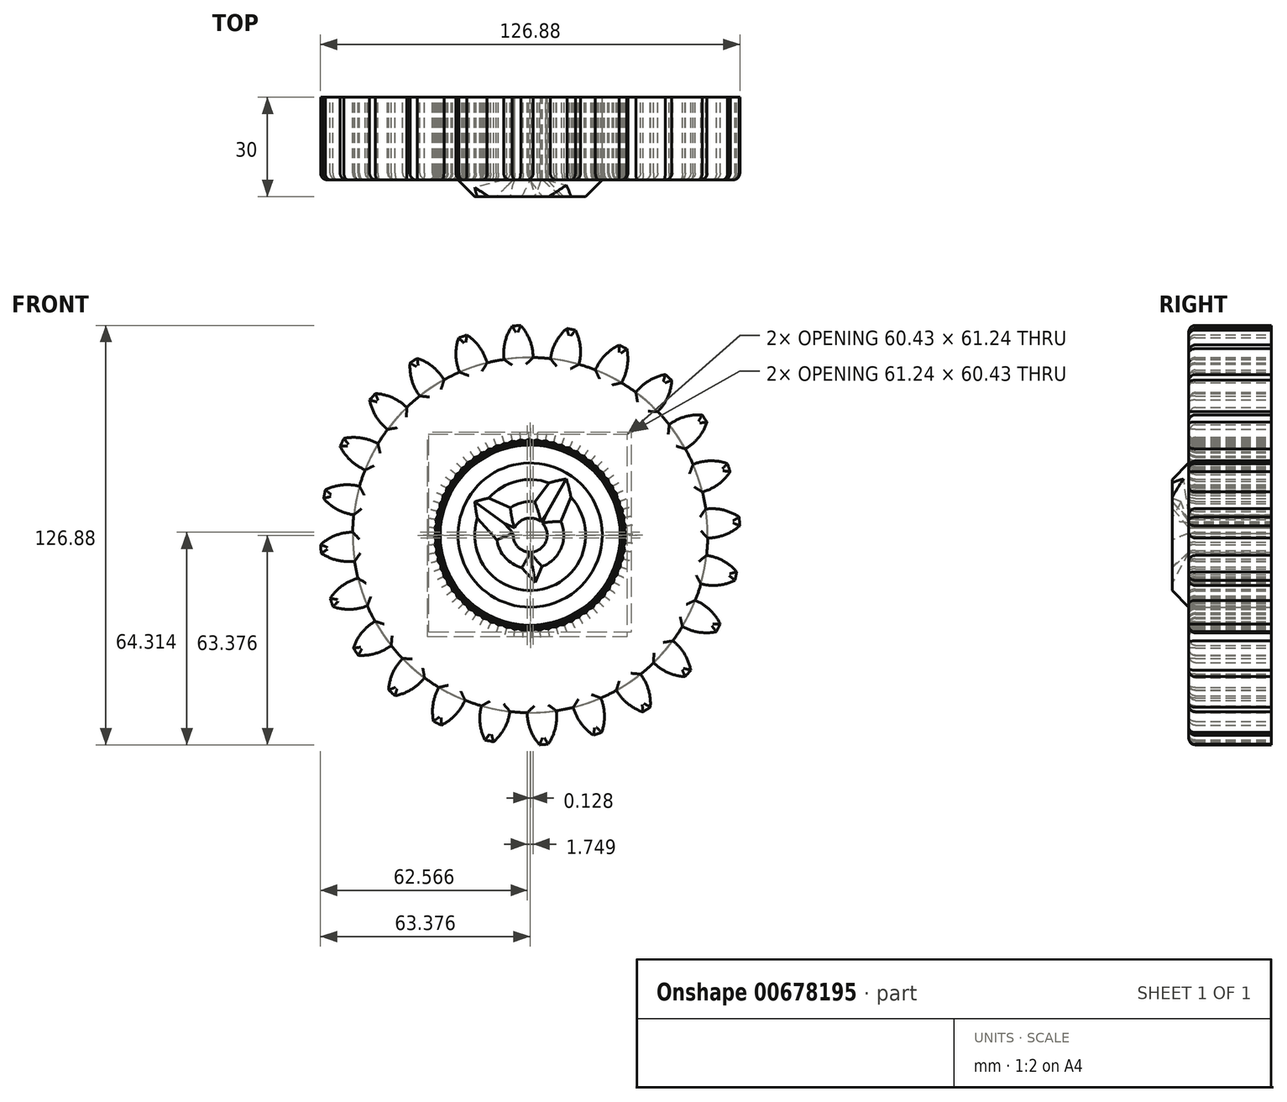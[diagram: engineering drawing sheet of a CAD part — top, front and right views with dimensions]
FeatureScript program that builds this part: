
annotation { "Feature Type Name" : "Feature", "Feature Type Description" : "" }
export const myFeature = defineFeature(function(context is Context, id is Id, definition is map)
    precondition{}
    {
        {
            var Q0;
            Q0=qCreatedBy(makeId("Front.planeOp"),FACE);
            var sketch = newSketch(context, id + "F0", { "sketchPlane" : qUnion([Q0])});
            skCircle(sketch, "E0", {"center": v(0, 0) * mm, "radius": 53.72 * mm});
            skCircle(sketch, "E1", {"center": v(0, 0) * mm, "radius": 58.67 * mm, "construction": true});
            skCircle(sketch, "E2", {"center": v(0, 0) * mm, "radius": 63.5 * mm, "construction": true});
            skLineSegment(sketch, "E3", {"start": v(0, 0) * mm, "end": v(0, 72.49) * mm, "construction": true});
            skLineSegment(sketch, "E4", {"start": v(0, 0) * mm, "end": v(-5.24, 80.02) * mm, "construction": true});
            skLineSegment(sketch, "E5", {"start": v(0, 58.67) * mm, "end": v(-56.45, 58.67) * mm, "construction": true});
            skLineSegment(sketch, "E6", {"start": v(0, 58.67) * mm, "end": v(-56.45, 38.13) * mm, "construction": true});
            skCircle(sketch, "E7", {"center": v(0, 0) * mm, "radius": 55.14 * mm, "construction": true});
            skCircle(sketch, "E8", {"center": v(0, 58.67) * mm, "radius": 14.6 * mm, "construction": true});
            skCircle(sketch, "E9", {"center": v(-13.72, 53.68) * mm, "radius": 14.6 * mm, "construction": true});
            skArc(sketch, "E10", {"start": v(0, 58.67) * mm, "mid": v(-1.2, 61.19) * mm, "end": v(-2.86, 63.44) * mm});
            skArc(sketch, "E11", {"start": v(0.88, 53.71) * mm, "mid": v(0.66, 56.23) * mm, "end": v(0, 58.67) * mm});
            skArc(sketch, "E12.MirrorCS", {"start": v(-7.66, 58.17) * mm, "mid": v(-6.8, 60.82) * mm, "end": v(-5.45, 63.27) * mm});
            skArc(sketch, "E13.MirrorCS", {"start": v(-7.88, 53.14) * mm, "mid": v(-8, 55.67) * mm, "end": v(-7.66, 58.17) * mm});
            skArc(sketch, "E14", {"start": v(-5.45, 63.27) * mm, "mid": v(-4.15, 63.33) * mm, "end": v(-2.86, 63.44) * mm});
            skCircle(sketch, "E15", {"center": v(0, 0) * mm, "radius": 21.8 * mm});
            skLineSegment(sketch, "E16", {"start": v(0, 0) * mm, "end": v(4.78, 6.29) * mm});
            skLineSegment(sketch, "E17", {"start": v(4.78, 6.29) * mm, "end": v(0, -5.17) * mm});
            skLineSegment(sketch, "E18", {"start": v(0, -5.17) * mm, "end": v(-7.89, 3.58) * mm});
            skLineSegment(sketch, "E19", {"start": v(-7.89, 3.58) * mm, "end": v(0, 0) * mm});
            skCircle(sketch, "E20.cCircle", {"center": v(0, 0) * mm, "radius": 27.22 * mm, "construction": true});
            skLineSegment(sketch, "E20.0", {"start": v(-28.82, -2.87) * mm, "end": v(-23.92, 16.33) * mm});
            skLineSegment(sketch, "E20.1", {"start": v(-23.92, 16.33) * mm, "end": v(-7.83, 27.89) * mm});
            skLineSegment(sketch, "E20.2", {"start": v(-7.83, 27.89) * mm, "end": v(11.93, 26.4) * mm});
            skLineSegment(sketch, "E20.3", {"start": v(11.93, 26.4) * mm, "end": v(26.1, 12.55) * mm});
            skLineSegment(sketch, "E20.4", {"start": v(26.1, 12.55) * mm, "end": v(28.06, -7.16) * mm});
            skLineSegment(sketch, "E20.5", {"start": v(28.06, -7.16) * mm, "end": v(16.9, -23.53) * mm});
            skLineSegment(sketch, "E20.6", {"start": v(16.9, -23.53) * mm, "end": v(-2.18, -28.88) * mm});
            skLineSegment(sketch, "E20.7", {"start": v(-2.18, -28.88) * mm, "end": v(-20.24, -20.72) * mm});
            skLineSegment(sketch, "E20.8", {"start": v(-20.24, -20.72) * mm, "end": v(-28.82, -2.87) * mm});
            skPoint(sketch, "E20.0.midPoint", {"position": v(-26.37, 6.73) * mm});
            skCircle(sketch, "E21", {"center": v(0, 0) * mm, "radius": 5.16 * mm});
            skSolve(sketch);
        }
        {
            var Q0;
            {var subQ0=sQuery(id+"F0.wireOp",EDGE,"E0");var subQ1=makeQuery(id+"F0.imprint","INTERSECT",VERTEX,{"derivedFrom":[subQ0,sQuery(id+"F0.wireOp",EDGE,"E11")]});Q0=makeQuery(id+"F0.imprint","IMPRINT",FACE,{"disambiguationData":[TD([[makeQuery(id+"F0.imprint","IMPRINT",EDGE,{"disambiguationData":[TD([[subQ1,-1.0]])],"derivedFrom":subQ0}),1.0]])]});}
            var Q1;
            Q1=makeQuery(id+"F0.imprint","IMPRINT",FACE,{"disambiguationData":[TD([[makeQuery(id+"F0.imprint","IMPRINT",EDGE,{"derivedFrom":sQuery(id+"F0.wireOp",EDGE,"E10")}),1.0]])]});
            extrude(context, id + "F1", {"entities" : qUnion([Q0, Q1]), "depth" : 25 * mm, "offsetDistance" : 25 * mm});
        }
        {
            var Q0;
            Q0=makeQuery(id+"F1.opExtrude","SWEPT_BODY",BODY,{"disambiguationData":[OSD([sQuery(id+"F0.wireOp",EDGE,"E0"),sQuery(id+"F0.wireOp",EDGE,"E10"),sQuery(id+"F0.wireOp",EDGE,"E11"),sQuery(id+"F0.wireOp",EDGE,"E12.MirrorCS"),sQuery(id+"F0.wireOp",EDGE,"E13.MirrorCS"),sQuery(id+"F0.wireOp",EDGE,"E14")])]});
            var Q1;
            Q1=makeQuery(id+"F1.opExtrude","SWEPT_FACE",FACE,{"disambiguationData":[OSD([sQuery(id+"F0.wireOp",EDGE,"E0")])]});
            circularPattern(context, id + "F2", {"entities" : qUnion([Q0]), "axis" : qUnion([Q1]), "angle" : 360 * degree, "instanceCount" : 24, "equalSpace" : true});
        }
        {
            var Q0;
            Q0=makeQuery(id+"F0.imprint","IMPRINT",FACE,{"disambiguationData":[TD([[makeQuery(id+"F0.imprint","IMPRINT",EDGE,{"derivedFrom":sQuery(id+"F0.wireOp",EDGE,"E15")}),1.0]])]});
            extrude(context, id + "F3", {"entities" : qUnion([Q0]), "operationType" : NewBodyOperationType.ADD, "depth" : 30 * mm, "offsetDistance" : 25 * mm});
        }
        {
            var Q0;
            Q0=makeQuery(id+"F3.opExtrude","CAP_FACE",FACE,{"disambiguationData":[OSD([sQuery(id+"F0.wireOp",EDGE,"E15"),sQuery(id+"F0.wireOp",EDGE,"E16"),sQuery(id+"F0.wireOp",EDGE,"E17"),sQuery(id+"F0.wireOp",EDGE,"E18"),sQuery(id+"F0.wireOp",EDGE,"E19")])],"isStart":false});
            chamfer(context, id + "F4", {"entities" : qUnion([Q0]), "width" : 5 * mm, "tangentPropagation" : true});
        }
        {
            var Q0;
            {var subQ0=makeQuery(id+"F1.opExtrude","CAP_FACE",FACE,{"disambiguationData":[OSD([sQuery(id+"F0.wireOp",EDGE,"E0"),sQuery(id+"F0.wireOp",EDGE,"E10"),sQuery(id+"F0.wireOp",EDGE,"E11"),sQuery(id+"F0.wireOp",EDGE,"E12.MirrorCS"),sQuery(id+"F0.wireOp",EDGE,"E13.MirrorCS"),sQuery(id+"F0.wireOp",EDGE,"E14"),sQuery(id+"F0.wireOp",EDGE,"E15")])],"isStart":false});Q0=makeQuery(id+"F3.boolean.opBoolean","MERGE",FACE,{"derivedFrom":[subQ0,makeQuery(id+"F2.opPattern","COPY",FACE,{"derivedFrom":subQ0,"instanceName":"1"}),makeQuery(id+"F2.opPattern","COPY",FACE,{"derivedFrom":subQ0,"instanceName":"2"}),makeQuery(id+"F2.opPattern","COPY",FACE,{"derivedFrom":subQ0,"instanceName":"3"}),makeQuery(id+"F2.opPattern","COPY",FACE,{"derivedFrom":subQ0,"instanceName":"4"}),makeQuery(id+"F2.opPattern","COPY",FACE,{"derivedFrom":subQ0,"instanceName":"5"}),makeQuery(id+"F2.opPattern","COPY",FACE,{"derivedFrom":subQ0,"instanceName":"6"}),makeQuery(id+"F2.opPattern","COPY",FACE,{"derivedFrom":subQ0,"instanceName":"7"}),makeQuery(id+"F2.opPattern","COPY",FACE,{"derivedFrom":subQ0,"instanceName":"8"}),makeQuery(id+"F2.opPattern","COPY",FACE,{"derivedFrom":subQ0,"instanceName":"9"}),makeQuery(id+"F2.opPattern","COPY",FACE,{"derivedFrom":subQ0,"instanceName":"10"}),makeQuery(id+"F2.opPattern","COPY",FACE,{"derivedFrom":subQ0,"instanceName":"11"}),makeQuery(id+"F2.opPattern","COPY",FACE,{"derivedFrom":subQ0,"instanceName":"12"}),makeQuery(id+"F2.opPattern","COPY",FACE,{"derivedFrom":subQ0,"instanceName":"13"}),makeQuery(id+"F2.opPattern","COPY",FACE,{"derivedFrom":subQ0,"instanceName":"14"}),makeQuery(id+"F2.opPattern","COPY",FACE,{"derivedFrom":subQ0,"instanceName":"15"}),makeQuery(id+"F2.opPattern","COPY",FACE,{"derivedFrom":subQ0,"instanceName":"16"}),makeQuery(id+"F2.opPattern","COPY",FACE,{"derivedFrom":subQ0,"instanceName":"17"}),makeQuery(id+"F2.opPattern","COPY",FACE,{"derivedFrom":subQ0,"instanceName":"18"}),makeQuery(id+"F2.opPattern","COPY",FACE,{"derivedFrom":subQ0,"instanceName":"19"}),makeQuery(id+"F2.opPattern","COPY",FACE,{"derivedFrom":subQ0,"instanceName":"20"}),makeQuery(id+"F2.opPattern","COPY",FACE,{"derivedFrom":subQ0,"instanceName":"21"}),makeQuery(id+"F2.opPattern","COPY",FACE,{"derivedFrom":subQ0,"instanceName":"22"}),makeQuery(id+"F2.opPattern","COPY",FACE,{"derivedFrom":subQ0,"instanceName":"23"})]});}
            fillet(context, id + "F5", {"entities" : qUnion([Q0]), "radius" : 2 * mm, "tangentPropagation" : true, "allowEdgeOverflow" : false});
        }
    });
